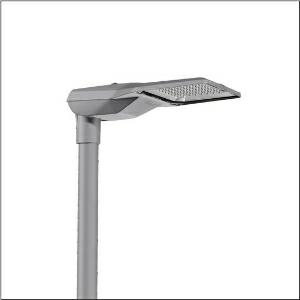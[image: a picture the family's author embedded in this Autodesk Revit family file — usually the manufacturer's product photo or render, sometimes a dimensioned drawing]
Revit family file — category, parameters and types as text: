
# Revit family: streetlight_sl_21_midi___st0_8a_5xe3c33s08mb_531e
name_source: partatom
category: Lighting Fixtures
units: mm (PartAtom-declared; Revit-internal decimal feet)

## family parameters
Cut with Voids When Loaded = No
Host = Face
Light Source = No
Part Type = Normal
Room Calculation Point = No
Round Connector Dimension = Use Diameter
Shared = No

## types (1)
- --- (1 x LED, 18270 lm, 136 W, 3000K)
    Apparent Load = 136 VA
    CIE Flux Codes = 38 75 97 100 100
    Color Rendering = 70
    Color Temperature = 3000K
    Default Elevation = 1800 mm
    Description = Streetlight SL 21 midi, mast luminaire, primary light control with lens, of PMMA, primary optical cover: cover, of toughened safety glass, transparent, light distribution: ST0.8a, light emission: direct distribution, primary light characteristic: asymmetric, installation type: side-entry, post-top, LED, High Power LED, rated luminous flux: 18.270lm, luminous efficacy: 134lm/W, light colour: 730, colour temperature: 3000K, control gear: D4i, control: overheat protection, constant luminous flux control, time-dependent luminous flux control, flexible luminous flux parameterisation, pre-setting: logarithmic dimming characteristic, mains connection: 230..240V, AC, 50/60Hz, start of lifetime: 136W, end of service life: 142W, reduction: 61W, luminaire housing, of diecast aluminium, powder-coated, Siteco® metallic grey (DB 702S), corrosivity category C5 mid according to DIN EN ISO 12944, please order mast flange separately, inclination adjustable: 0°, 5°, 10°, 15°, sealing non-destructively replaceable, multi-level sealing system, length: 644mm, width: 335mm, height: 110mm, mast flange for spigot size: 42mm (side-entry): 5XC10008XM4, 60/48mm (side-entry/post-top): 5XC10108XM2, 76/60mm (side-entry/post-top): 5XC10108XM1, mounting height: 4..8m, Smart Interface above, protection rating (complete): IP66, insulation class (complete): insulation class II (safety insulation), certification: CE, ENEC, ENEC+, VDE, impact resistance: IK10, permissible operating ambient temperature for outdoor applications: -40..+50°C, standard-compliant lighting for roads and squares, packaging unit: 1 piece

Light Distribution: ST0.8a
    Height = 111 mm
    Lamp = 1 x LED
    Lamp Light Flux = 18270 lm
    Lamp Power = 136 W
    Lamp count = 1
    Length = 644 mm
    Luminous efficacy = 134 lm/W
    Manufacturer = Siteco
    ModVariant = No
    Model = 5XE3C33S08MB
    Number of Poles = 1
    OnlyDefault = Yes
    Power Factor = 1
    Product Name = Streetlight SL 21 midi | ST0.8a
    Product group = mast luminaire | pylon top
    ProductGroupID = 6100
    Protection Class = Protection class II
    Protection Degree = IP 66
    RLX_Detail_Level = 1
    RLX_Emergency_Light_Flux = 0 lm
    RLX_Emergency_Type = 0
    RLX_Emergency_Type_DB = No
    RlxData = <blob elided: 26865 chars, md5=de5b23a4>
    Socket = socket
    Standby Power = 0 W
    System Light Flux = 18270 lm
    System Power = 136 W
    Type Comments = factory setting: luminous flux: 100 % | dim-lin: 254 | 695 mA
    Type Image = l_1004302.jpg
    URL = http://relux.com
    VarID = @adj_186104
    Voltage = 0 V
    Weight = 0.00 kg
    Width = 336 mm

## geometry (parser evidence)
native form markers: Blend x4, Sweep x12
no freeform markers — native parametric forms only
